# Revit family: Domino Touch 2EV 30
name_source: partatom
category: Equipamento especial
revit_build: Autodesk Revit 2016 (Build: 20150220_1215(x64)
units: mm (PartAtom-declared; Revit-internal decimal feet)

## family parameters
Com base no plano de trabalho = Não
Compartilhado = Não
Corte com vazios quando carregados = Não
Cota do conector redondo = Utilizar diâmetro
Ponto de cálculo do ambiente = Não
Sempre na vertical = Sim
Tipo de parte = Normal

## types (1)
- Tramontina - Domino Touch 2EV 30
    Classe de Construção = Classe 1
    Consumo máximo = 3,0 kWh
    Código de montagem = 94748/220
    Descrição = Tramontina Cooktop Vitrocerâmico
    Desenvolvedor = Factory Cursos & Desenvolvimento
    Disjuntor termomagnético = 32 A
    Fabricante = Tramontina
    Frequência = 50 - 60 Hz
    Grau de Proteção = IPX0
    Modelo = Tramontina - Dominó Touch 2 EV 30
    Peso Bruto = 6,2 kg
    Peso liquido = 4,7 kg
    Potência das áreas de aquecimento - 200 mm Diametro = 1,8 kW (2x)
    Potência máxima = 3,0 kW
    Potência áreas de aquecimento - 165 mm Diametro = 1,2 kW (2x)
    Site do desenvolvedor = www.factorycursos.com.br
    Tensão = 220 V
    Tipo de imagem = 94748 220.jpg
    Tramontina Ref = Tramontina - 94748/220 - C
    URL = www.tramontina.com.br
